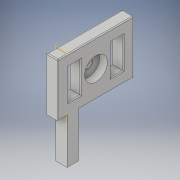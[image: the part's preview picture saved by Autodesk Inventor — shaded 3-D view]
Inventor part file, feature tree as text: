
AUTODESK INVENTOR PART (.ipt)
format: ipt  version: 2017 (Build 210142000, 142)  size: 199,168 bytes
history: native  units: in
note: dims shown in document units (in); Inventor stores cm internally (conversion verified against a paired STEP export)
features: sketch x4, extrude x4, projected_geometry x3, hole x1, fillet x1, plane x1
ambient origin geometry x8: Origin, YZ Plane, XZ Plane, XY Plane, X Axis, Y Axis, Z Axis, Center Point
bodies: Solid1 (feature_tree)
feature tree (14):
  sketch  "Sketch1"  dims[d8=0.51in d9=0.1975in]
  extrude  "Extrusion1"  Depth=0.1975in
  extrude  "Extrusion2"  Depth=0.1825in
  extrude  "Extrusion5"  Depth=0.375in
  hole  "Hole1"  [1 undecoded]
  fillet  "Fillet1"  Radius=0.1825in
  plane  "Work Plane1"
  extrude  "Extrusion6"  Depth=0.1775in
  sketch  "Sketch2"  dims[d10=0.1775in d11=0.1825in]
  projected_geometry  "Projected Loop1"
  sketch  "Sketch5"  dims[d12=0.1875in d13=0.0in d14=0.375in]
  projected_geometry  "Projected Loop6"
  sketch  "Sketch7"  dims[d15=0.4375in d17=0.125in d18=0.0in d28=0.1825in d29=0.1775in d31=0.247in d32=0.1235in d37=1.25in d38=1.25in d39=0.875in d43=0.1975in d48=0.51in d49=0.1825in d50=1.0in d51=0.0in d52=1.25in d53=0.625in d54=0.145in d55=0.38in d56=0.375in d57=0.25in d58=0.5635in d59=0.588in d60=0.8108in d61=0.015in d74=-0.15in d75=0.1875in d76=0.75in d77=0.1875in d78=0.0in]
  projected_geometry  "Projected Loop8"
note: 1 required parameter value undecoded (feature->parameter linkage not recoverable at this tier; creation-order binding heuristic only, values carry confidence <= 0.55)
